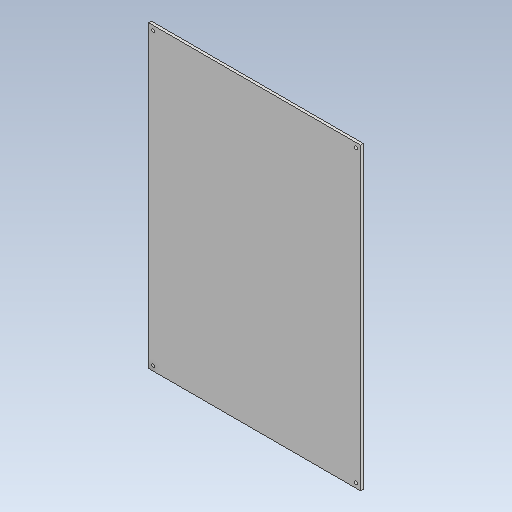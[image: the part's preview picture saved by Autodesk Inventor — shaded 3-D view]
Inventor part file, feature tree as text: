
AUTODESK INVENTOR PART (.ipt)
format: ipt  version: 2020 (Build 240168000, 168)  size: 95,232 bytes
history: native  units: mm
features: sketch x2, extrude x1, hole x1
ambient origin geometry x8: Origin, YZ Plane, XZ Plane, XY Plane, X Axis, Y Axis, Z Axis, Center Point
bodies: Solid1 (feature_tree)
feature tree (4):
  extrude  "Extrusion1"  Depth=325.0mm
  hole  "Hole1"  [1 undecoded]
  sketch  "Sketch1"  dims[d0=230.0mm d1=325.0mm]
  sketch  "Sketch2"  dims[d2=3.0mm d3=0.0mm d4=5.0mm d5=5.0mm d6=3.5mm d7=6.0mm d8=4.0mm d9=2.0mm d10=90.0deg d11=21.0mm d12=0.0mm]
note: 1 required parameter value undecoded (feature->parameter linkage not recoverable at this tier; creation-order binding heuristic only, values carry confidence <= 0.55)
